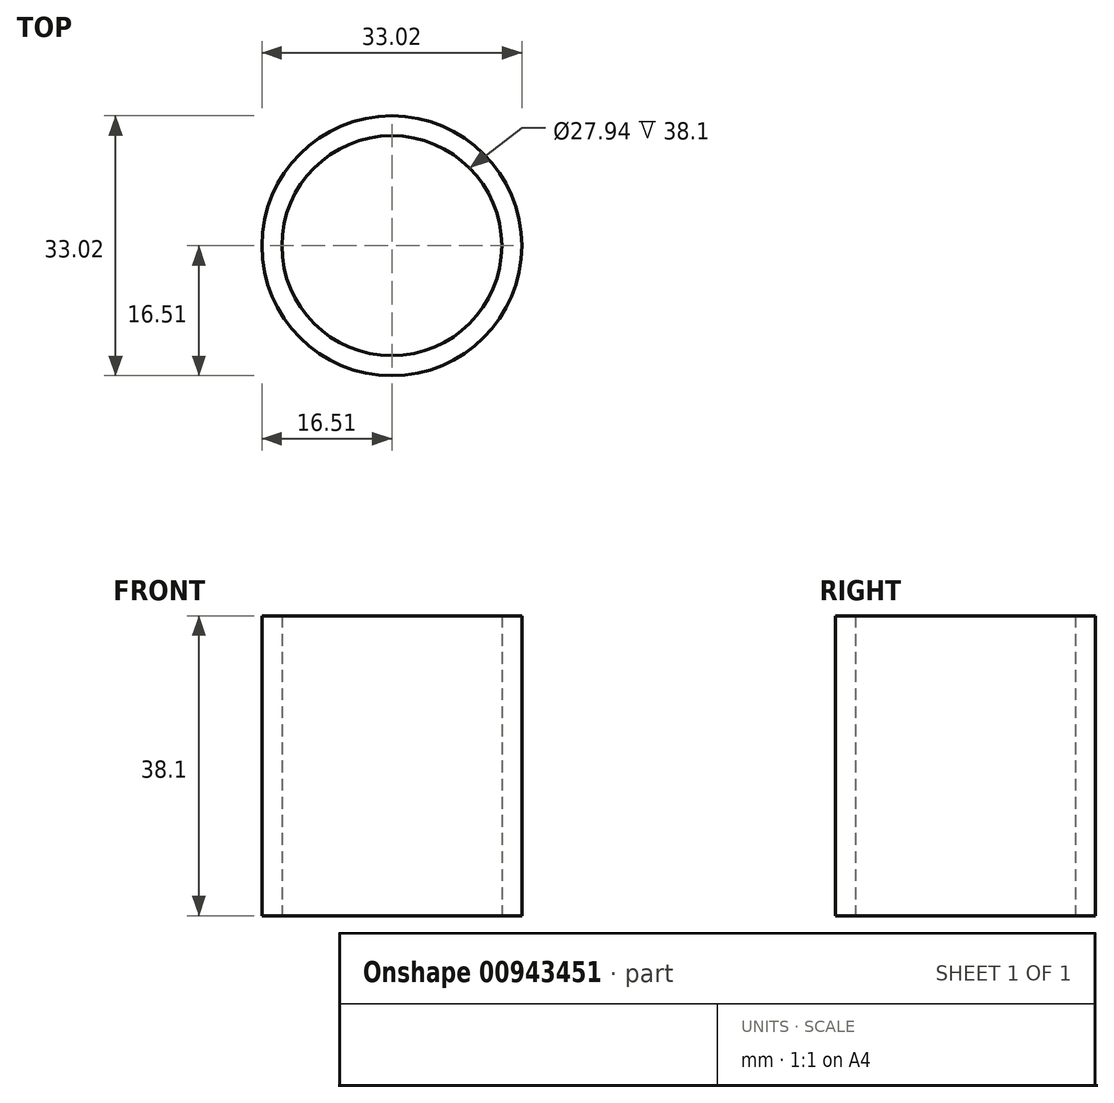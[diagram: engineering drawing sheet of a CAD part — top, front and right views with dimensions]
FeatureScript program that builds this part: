
annotation { "Feature Type Name" : "Feature", "Feature Type Description" : "" }
export const myFeature = defineFeature(function(context is Context, id is Id, definition is map)
    precondition{}
    {
        {
            var Q0;
            Q0=qCreatedBy(makeId("Top.planeOp"),FACE);
            var sketch = newSketch(context, id + "F0", { "sketchPlane" : qUnion([Q0])});
            skCircle(sketch, "E0", {"center": v(0, 0) * mm, "radius": 16.51 * mm});
            skCircle(sketch, "E1", {"center": v(0, 0) * mm, "radius": 13.97 * mm});
            skSolve(sketch);
        }
        {
            var Q0;
            Q0 = qSketchRegion(id + "F0", true);
            extrude(context, id + "F1", {"entities" : qUnion([Q0]), "depth" : 38.1 * mm, "offsetDistance" : 25.4 * mm});
        }
    });
